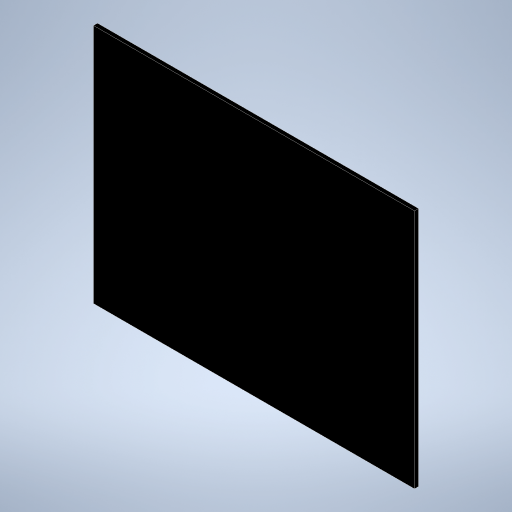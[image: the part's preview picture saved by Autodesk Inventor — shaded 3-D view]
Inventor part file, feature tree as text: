
AUTODESK INVENTOR PART (.ipt)
format: ipt  version: 2023 (Build 270158000, 158)  size: 198,656 bytes
history: native  units: mm
features: other x1, extrude x1, sketch x1
ambient origin geometry x8: Origin, YZ Plane, XZ Plane, XY Plane, X Axis, Y Axis, Z Axis, Center Point
bodies: Body1 (feature_tree)
feature tree (3):
  other  "ソリッド1"
  extrude  "押し出し1"  Depth=400.0mm
  sketch  "スケッチ1"
